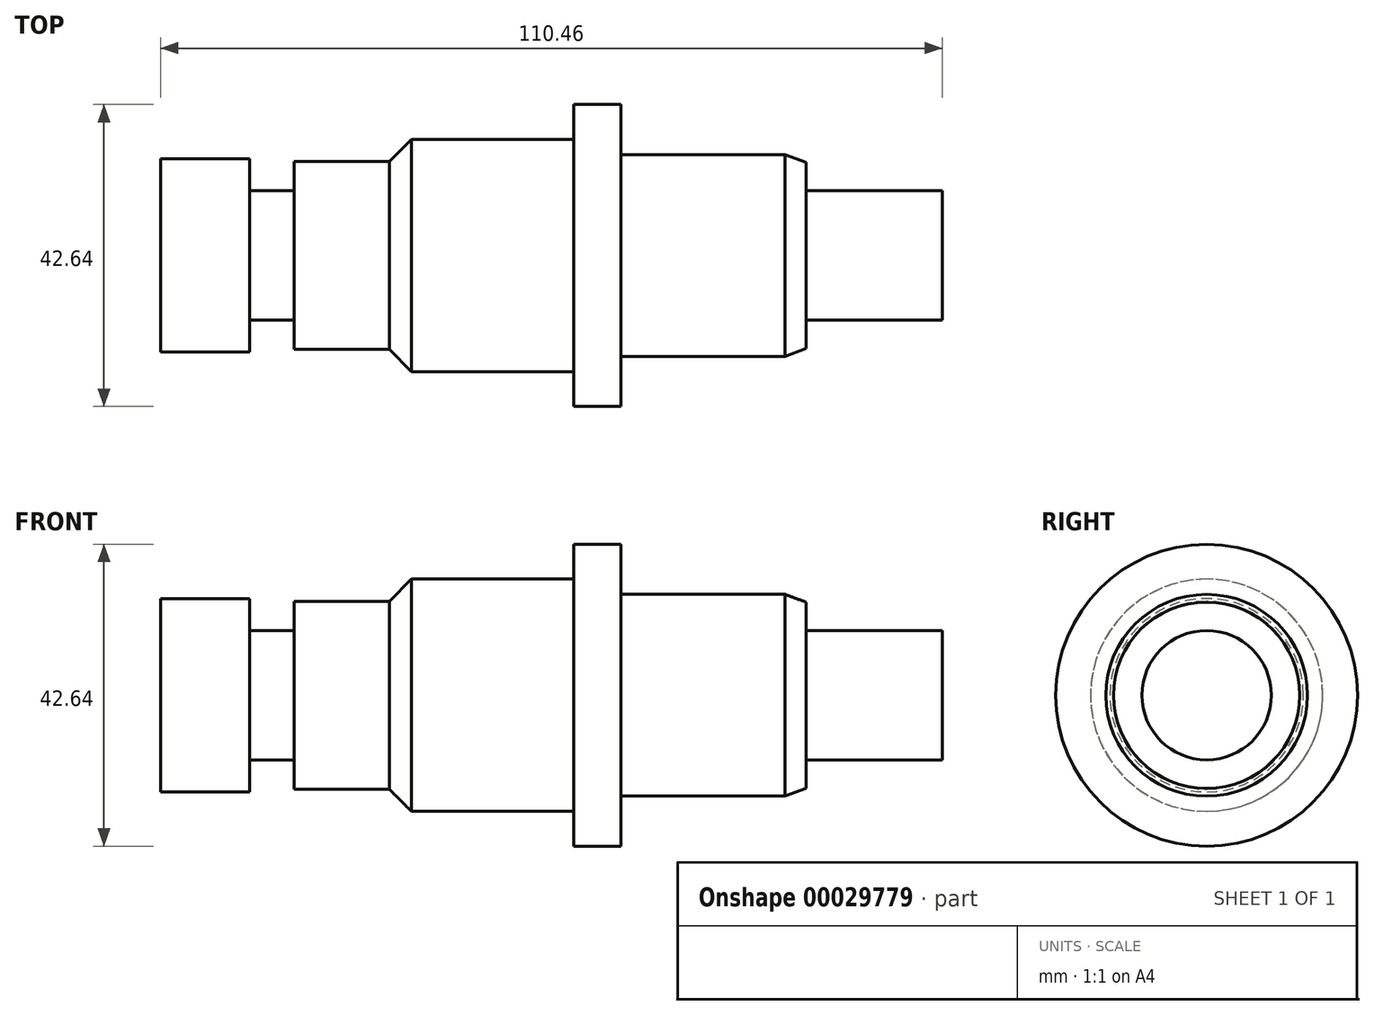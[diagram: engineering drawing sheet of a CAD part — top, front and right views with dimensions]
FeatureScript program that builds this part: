
annotation { "Feature Type Name" : "Feature", "Feature Type Description" : "" }
export const myFeature = defineFeature(function(context is Context, id is Id, definition is map)
    precondition{}
    {
        {
            var Q0;
            Q0=qCreatedBy(makeId("Top.planeOp"),FACE);
            var sketch = newSketch(context, id + "F0", { "sketchPlane" : qUnion([Q0])});
            skLineSegment(sketch, "E0", {"start": v(0, 0) * mm, "end": v(110.46, 0) * mm});
            skLineSegment(sketch, "E1", {"start": v(110.46, 0) * mm, "end": v(110.46, 9.14) * mm});
            skLineSegment(sketch, "E2", {"start": v(110.46, 9.14) * mm, "end": v(91.2, 9.14) * mm});
            skLineSegment(sketch, "E3", {"start": v(91.2, 9.14) * mm, "end": v(91.2, 14.25) * mm});
            skLineSegment(sketch, "E4", {"start": v(91.2, 14.25) * mm, "end": v(65.06, 14.25) * mm});
            skLineSegment(sketch, "E5", {"start": v(65.06, 14.25) * mm, "end": v(65.06, 21.32) * mm});
            skLineSegment(sketch, "E6", {"start": v(65.06, 21.32) * mm, "end": v(58.37, 21.32) * mm});
            skLineSegment(sketch, "E7", {"start": v(58.37, 21.32) * mm, "end": v(58.37, 16.41) * mm});
            skLineSegment(sketch, "E8", {"start": v(58.37, 16.41) * mm, "end": v(30.46, 16.41) * mm});
            skLineSegment(sketch, "E9", {"start": v(30.46, 16.41) * mm, "end": v(30.46, 13.27) * mm});
            skLineSegment(sketch, "E10", {"start": v(30.46, 13.27) * mm, "end": v(18.87, 13.27) * mm});
            skLineSegment(sketch, "E11", {"start": v(18.87, 13.27) * mm, "end": v(18.87, 9.14) * mm});
            skLineSegment(sketch, "E12", {"start": v(18.87, 9.14) * mm, "end": v(12.58, 9.14) * mm});
            skLineSegment(sketch, "E13", {"start": v(12.58, 9.14) * mm, "end": v(12.58, 13.66) * mm});
            skLineSegment(sketch, "E14", {"start": v(12.58, 13.66) * mm, "end": v(0, 13.66) * mm});
            skLineSegment(sketch, "E15", {"start": v(0, 13.66) * mm, "end": v(0, 0) * mm});
            skSolve(sketch);
        }
        {
            var Q0;
            Q0 = qSketchRegion(id + "F0", true);
            var Q1;
            Q1 = qSketchRegion(id + "FthWt4bMuUWZRW3_1", true);
            var Q2;
            Q2=sQuery(id+"F0.wireOp",EDGE,"E0");
            revolve(context, id + "F1", {"entities" : qUnion([Q0, Q1]), "axis" : qUnion([Q2]), "revolveType" : RevolveType.FULL});
        }
        {
            var Q0;
            Q0=makeQuery(id+"F1.opRevolve","SWEPT_EDGE",EDGE,{"disambiguationData":[OSD([sQuery(id+"F0.wireOp",EDGE,"E8"),sQuery(id+"F0.wireOp",EDGE,"E9")])]});
            chamfer(context, id + "F2", {"entities" : qUnion([Q0]), "chamferType" : ChamferType.OFFSET_ANGLE, "width" : 5 * mm, "oppositeDirection" : false, "angle" : 45 * degree, "tangentPropagation" : true});
        }
        {
            var Q0;
            Q0=makeQuery(id+"F1.opRevolve","SWEPT_EDGE",EDGE,{"disambiguationData":[OSD([sQuery(id+"F0.wireOp",EDGE,"E3"),sQuery(id+"F0.wireOp",EDGE,"E4")])]});
            chamfer(context, id + "F3", {"entities" : qUnion([Q0]), "chamferType" : ChamferType.OFFSET_ANGLE, "width" : 3 * mm, "oppositeDirection" : false, "angle" : 20 * degree, "tangentPropagation" : true});
        }
    });
